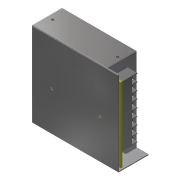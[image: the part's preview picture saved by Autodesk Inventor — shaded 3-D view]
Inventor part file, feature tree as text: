
AUTODESK INVENTOR PART (.ipt)
format: ipt  version: 2022 (Build 260153000, 153)  size: 473,088 bytes
history: native  units: mm
features: sketch x18, extrude x16, fillet x4, pattern_linear x2, projected_geometry x2, other x1, plane x1
ambient origin geometry x8: Origin, YZ Plane, XZ Plane, XY Plane, X Axis, Y Axis, Z Axis, Center Point
bodies: Solid2 (feature_tree)
feature tree (44):
  other  "Твердое тело1"
  extrude  "Выдавливание1"  Depth=97.0mm
  extrude  "Выдавливание2"  Depth=1.0mm
  extrude  "Выдавливание3"  Depth=34.0mm TaperAngle=0.0deg
  extrude  "Выдавливание5"  Depth=10.0mm
  extrude  "Выдавливание10"  Depth=15.0mm TaperAngle=0.0deg
  extrude  "Выдавливание11"  Depth=55.5mm
  pattern_linear  "Прямоуг.массив1"  Spacing1=51.5mm  [1 undecoded]
  extrude  "Выдавливание12"  Depth=51.5mm
  fillet  "Сопряжение1"  Radius=3.0mm
  extrude  "Выдавливание13"  Depth=45.5mm
  pattern_linear  "Прямоуг.массив2"  Spacing1=45.5mm  [1 undecoded]
  fillet  "Сопряжение2"  Radius=55.0mm
  fillet  "Сопряжение3"  Radius=20.5mm
  fillet  "Сопряжение4"  Radius=3.0mm
  extrude  "Выдавливание14"  Depth=10.0mm TaperAngle=0.0deg
  extrude  "Выдавливание15"  Depth=10.0mm
  extrude  "Выдавливание16"  Depth=74.0mm
  plane  "Work Plane1"
  extrude  "Extrusion17"  Depth=18.0mm
  extrude  "Extrusion18"  Depth=17.5mm
  extrude  "Extrusion19"  Depth=21.0mm
  extrude  "Extrusion20"  Depth=1.0mm TaperAngle=0.0deg
  extrude  "Extrusion21"  Depth=8.5mm
  sketch  "Sketch23"  dims[d15=55.5mm d16=20.5mm]
  sketch  "Sketch24"  dims[d17=3.0mm d18=51.5mm d19=51.5mm d20=3.0mm d21=45.5mm d22=45.5mm d23=55.0mm d24=20.5mm d27=3.0mm d28=0.0mm d41=3.0mm d42=0.0mm d43=3.0mm d44=74.0mm d45=18.0mm d46=17.5mm d47=21.0mm d48=1.0mm d49=0.0mm d50=90.0mm d52=8.5mm d53=7.0mm d54=80.0mm d56=8.5mm d57=10.0mm d59=10.0mm d61=4.0mm d62=0.0mm d63=1.0mm d64=2.0mm d65=0.0mm d66=80.0mm d68=8.5mm d69=1.0mm d70=1.0mm d71=1.0mm d72=84.0mm d73=0.0mm d74=0.001mm d75=0.0mm d76=0.1mm d77=0.1mm d78=0.1mm d79=0.1mm d80=0.001mm d81=0.0mm d82=2.0mm d83=2.0mm d84=0.0mm d85=2.0mm d86=0.0mm d87=0.0mm d88=0.0mm d89=0.0mm d90=0.0mm d91=10.0mm d92=0.0mm]
  sketch  "Эскиз1"
  sketch  "Эскиз2"
  sketch  "Эскиз3"
  sketch  "Эскиз5"
  sketch  "Эскиз8"
  sketch  "Эскиз9"
  sketch  "Эскиз10"
  sketch  "Эскиз11"
  sketch  "Эскиз12"
  sketch  "Эскиз13"
  sketch  "Эскиз15"
  sketch  "Sketch17"  dims[d0=99.0mm d1=97.0mm]
  sketch  "Sketch18"  dims[d2=35.0mm d3=0.0mm d4=1.0mm]
  sketch  "Sketch19"  dims[d5=13.0mm d6=34.0mm d7=0.0mm]
  projected_geometry  "Projected Loop1"
  sketch  "Sketch20"  dims[d8=67.0mm d9=10.0mm]
  sketch  "Sketch22"  dims[d10=2.0mm d11=15.0mm d12=0.0mm]
  projected_geometry  "Projected Loop2"
note: 2 required parameter values undecoded (feature->parameter linkage not recoverable at this tier; creation-order binding heuristic only, values carry confidence <= 0.55)
